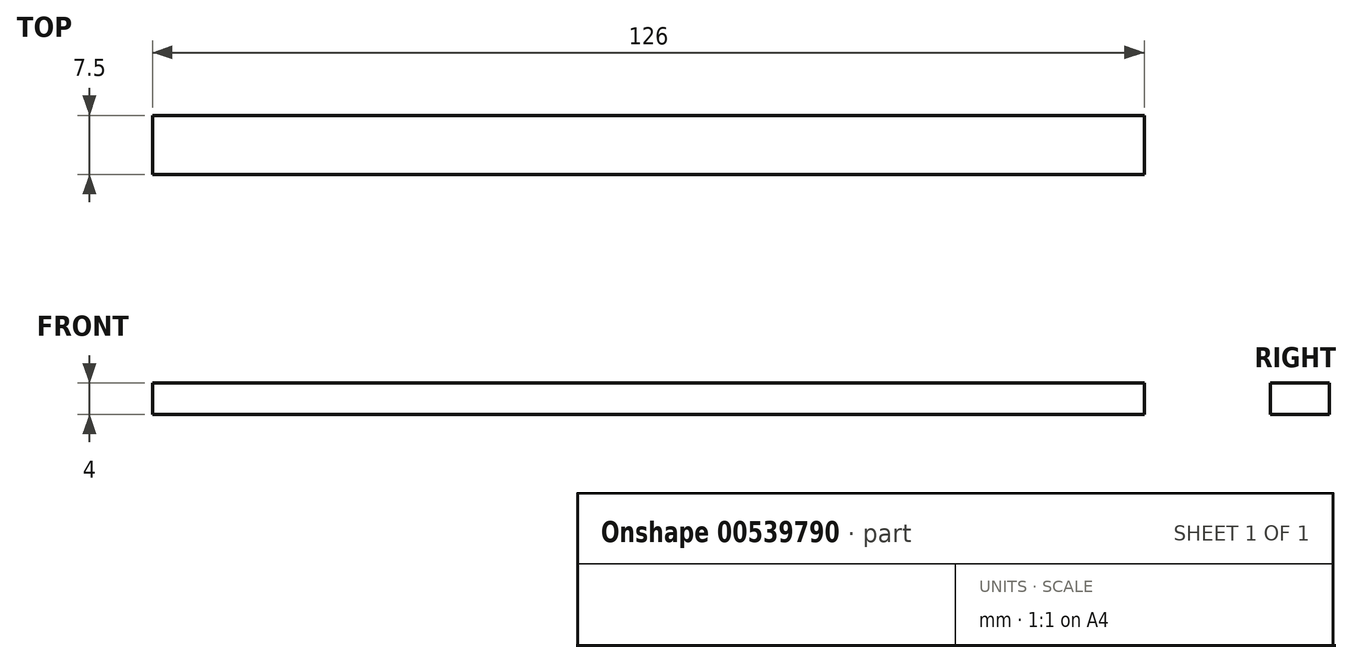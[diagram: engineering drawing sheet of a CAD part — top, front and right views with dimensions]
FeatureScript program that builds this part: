
annotation { "Feature Type Name" : "Feature", "Feature Type Description" : "" }
export const myFeature = defineFeature(function(context is Context, id is Id, definition is map)
    precondition{}
    {
        {
            var Q0;
            Q0=qCreatedBy(makeId("Top.planeOp"),FACE);
            var sketch = newSketch(context, id + "F0", { "sketchPlane" : qUnion([Q0])});
            skLineSegment(sketch, "E0.bottom", {"start": v(63, 3.75) * mm, "end": v(-63, 3.75) * mm});
            skLineSegment(sketch, "E0.top", {"start": v(63, -3.75) * mm, "end": v(-63, -3.75) * mm});
            skLineSegment(sketch, "E0.left", {"start": v(63, 3.75) * mm, "end": v(63, -3.75) * mm});
            skLineSegment(sketch, "E0.right", {"start": v(-63, 3.75) * mm, "end": v(-63, -3.75) * mm});
            skPoint(sketch, "E0.middle", {"position": v(0, 0) * mm});
            skSolve(sketch);
        }
        {
            var Q0;
            Q0 = qSketchRegion(id + "F0", true);
            extrude(context, id + "F1", {"entities" : qUnion([Q0]), "depth" : 4 * mm, "offsetDistance" : 25 * mm});
        }
    });
